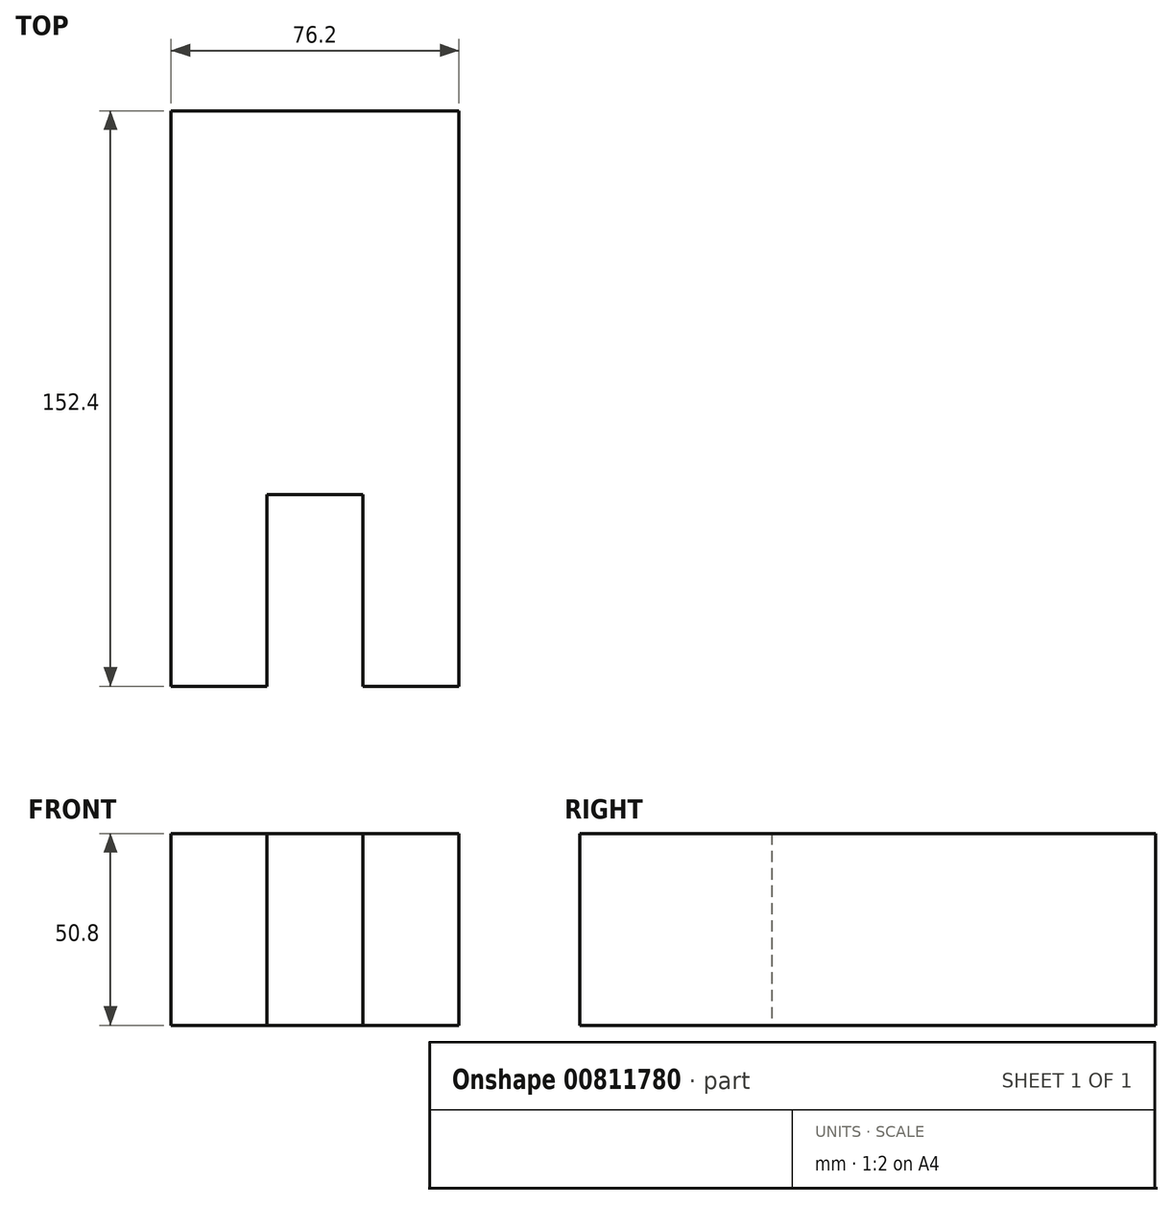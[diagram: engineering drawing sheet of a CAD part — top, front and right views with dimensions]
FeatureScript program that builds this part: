
annotation { "Feature Type Name" : "Feature", "Feature Type Description" : "" }
export const myFeature = defineFeature(function(context is Context, id is Id, definition is map)
    precondition{}
    {
        {
            var Q0;
            Q0=qCreatedBy(makeId("Top.planeOp"),FACE);
            var sketch = newSketch(context, id + "F0", { "sketchPlane" : qUnion([Q0])});
            skLineSegment(sketch, "E0", {"start": v(0, 0) * mm, "end": v(0, 152.4) * mm});
            skLineSegment(sketch, "E1", {"start": v(0, 0) * mm, "end": v(25.4, 0) * mm});
            skLineSegment(sketch, "E2", {"start": v(25.4, 0) * mm, "end": v(25.4, 50.8) * mm});
            skLineSegment(sketch, "E3", {"start": v(25.4, 50.8) * mm, "end": v(50.8, 50.8) * mm});
            skLineSegment(sketch, "E4", {"start": v(50.8, 50.8) * mm, "end": v(50.8, 0) * mm});
            skLineSegment(sketch, "E5", {"start": v(50.8, 0) * mm, "end": v(76.2, 0) * mm});
            skLineSegment(sketch, "E6", {"start": v(76.2, 0) * mm, "end": v(76.2, 152.4) * mm});
            skLineSegment(sketch, "E7", {"start": v(0, 152.4) * mm, "end": v(76.2, 152.4) * mm});
            skSolve(sketch);
        }
        {
            var Q0;
            Q0=makeQuery(id+"F0.imprint","IMPRINT",FACE,{"disambiguationData":[TD([[makeQuery(id+"F0.imprint","IMPRINT",EDGE,{"derivedFrom":sQuery(id+"F0.wireOp",EDGE,"E0")}),-1.0]])]});
            extrude(context, id + "F1", {"entities" : qUnion([Q0]), "depth" : 50.8 * mm, "offsetDistance" : 25.4 * mm});
        }
    });
